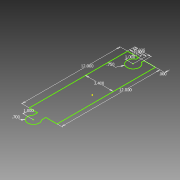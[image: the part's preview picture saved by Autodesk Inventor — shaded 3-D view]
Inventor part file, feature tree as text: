
AUTODESK INVENTOR PART (.ipt)
format: ipt  version: 2015 (Build 190159000, 159)  size: 71,680 bytes
history: native  units: in
note: dims shown in document units (in); Inventor stores cm internally (conversion verified against a paired STEP export)
features: sketch x1
ambient origin geometry x8: Origin, YZ Plane, XZ Plane, XY Plane, X Axis, Y Axis, Z Axis, Center Point
feature tree (1):
  sketch  "Sketch1"  dims[d0=3.4in d1=0.75in d2=0.7in d3=1.0in d4=1.0in d5=12.0in d6=12.0in d7=0.0in d8=1.375in d9=2.025in d10=1.7in]
